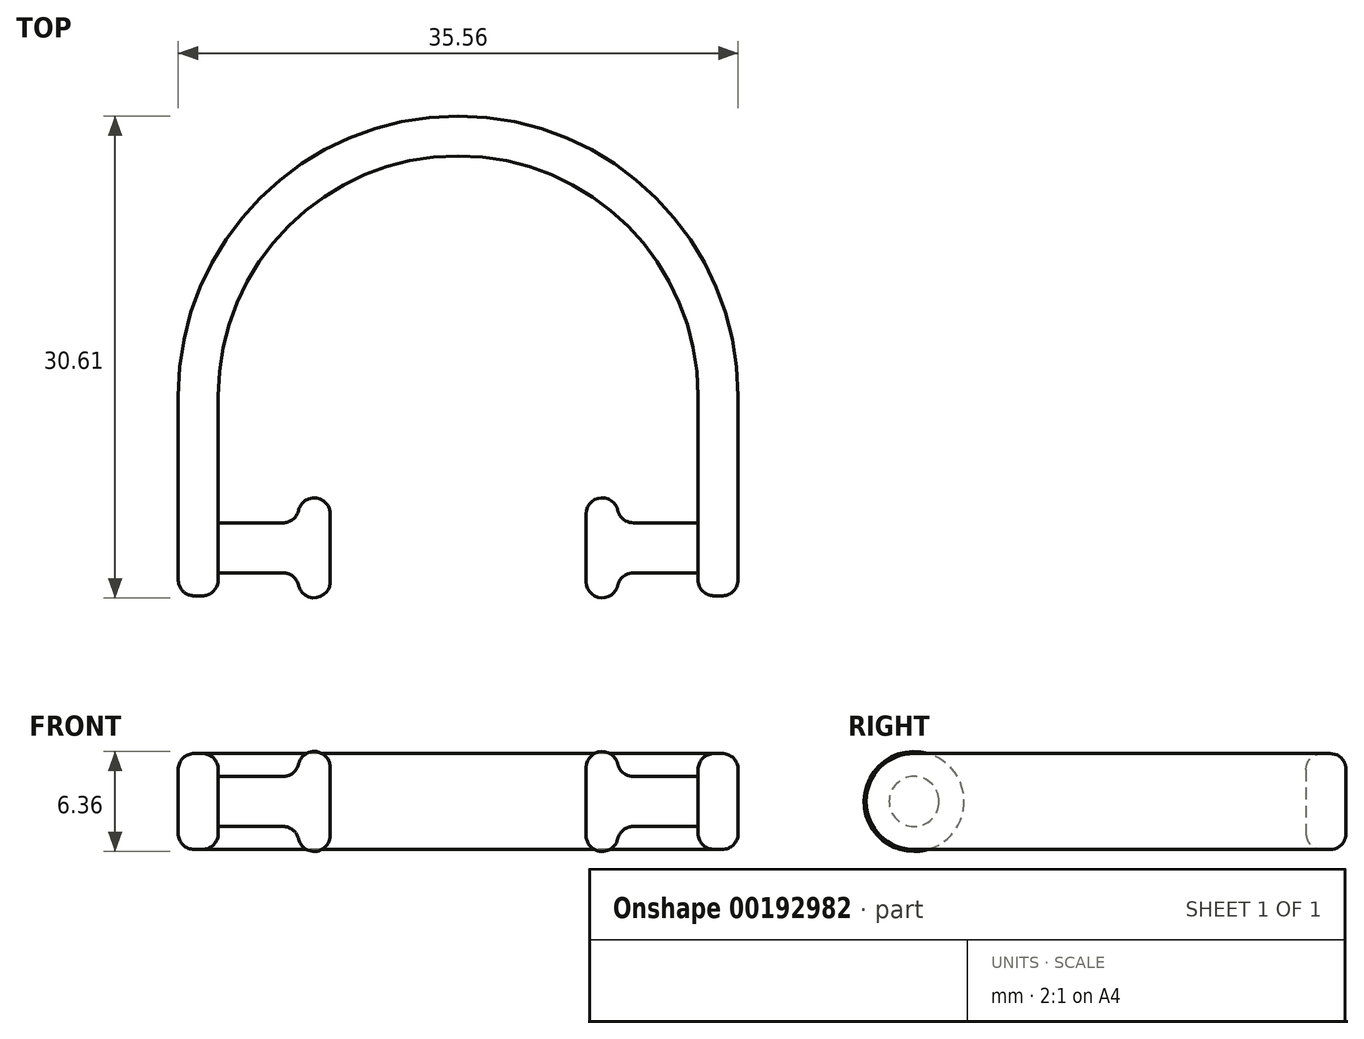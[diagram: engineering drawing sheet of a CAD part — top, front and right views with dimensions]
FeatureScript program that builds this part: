
annotation { "Feature Type Name" : "Feature", "Feature Type Description" : "" }
export const myFeature = defineFeature(function(context is Context, id is Id, definition is map)
    precondition{}
    {
        {
            var Q0;
            Q0=qCreatedBy(makeId("Top.planeOp"),FACE);
            var sketch = newSketch(context, id + "F0", { "sketchPlane" : qUnion([Q0])});
            skArc(sketch, "E0", {"start": v(-15.24, 9.65) * mm, "mid": v(0, 24.9) * mm, "end": v(15.24, 9.65) * mm});
            skLineSegment(sketch, "E1", {"start": v(-15.24, 9.65) * mm, "end": v(-15.24, -3.05) * mm});
            skLineSegment(sketch, "E2", {"start": v(-17.78, -3.05) * mm, "end": v(-17.78, 9.65) * mm});
            skLineSegment(sketch, "E3", {"start": v(0, 67.15) * mm, "end": v(0, -19.72) * mm, "construction": true});
            skLineSegment(sketch, "E4", {"start": v(-17.78, -3.05) * mm, "end": v(-15.24, -3.05) * mm});
            skLineSegment(sketch, "E5.MirrorCS", {"start": v(17.78, -3.05) * mm, "end": v(15.24, -3.05) * mm});
            skLineSegment(sketch, "E6.MirrorCS", {"start": v(15.24, 9.65) * mm, "end": v(15.24, -3.05) * mm});
            skLineSegment(sketch, "E7.MirrorCS", {"start": v(17.78, -3.05) * mm, "end": v(17.78, 9.65) * mm});
            skArc(sketch, "E8", {"start": v(-17.78, 9.65) * mm, "mid": v(0, 27.43) * mm, "end": v(17.78, 9.65) * mm});
            skSolve(sketch);
        }
        {
            var Q0;
            Q0=qSketchRegion(id+"F0",true);
            extrude(context, id + "F1", {"entities" : qUnion([Q0]), "endBound" : BoundingType.SYMMETRIC, "depth" : 6.1 * mm});
        }
        {
            var Q0;
            Q0=qCreatedBy(makeId("Top.planeOp"),FACE);
            var sketch = newSketch(context, id + "F2", { "sketchPlane" : qUnion([Q0])});
            skLineSegment(sketch, "E9", {"start": v(-15.24, 0) * mm, "end": v(-8.13, 0) * mm});
            skLineSegment(sketch, "E10", {"start": v(-8.13, 0) * mm, "end": v(-8.13, 3.18) * mm});
            skLineSegment(sketch, "E11", {"start": v(-8.13, 3.18) * mm, "end": v(-10.16, 3.18) * mm});
            skLineSegment(sketch, "E12", {"start": v(-10.16, 3.18) * mm, "end": v(-10.16, 1.59) * mm});
            skLineSegment(sketch, "E13", {"start": v(-10.16, 1.59) * mm, "end": v(-15.24, 1.59) * mm});
            skLineSegment(sketch, "E14", {"start": v(-15.24, 1.59) * mm, "end": v(-15.24, 0) * mm});
            skLineSegment(sketch, "E15", {"start": v(0, 27.07) * mm, "end": v(0, -22.76) * mm, "construction": true});
            skLineSegment(sketch, "E16.MirrorCS", {"start": v(15.24, 0) * mm, "end": v(8.13, 0) * mm});
            skLineSegment(sketch, "E17.MirrorCS", {"start": v(15.24, 1.59) * mm, "end": v(15.24, 0) * mm});
            skLineSegment(sketch, "E18.MirrorCS", {"start": v(10.16, 1.59) * mm, "end": v(15.24, 1.59) * mm});
            skLineSegment(sketch, "E19.MirrorCS", {"start": v(10.16, 3.18) * mm, "end": v(10.16, 1.59) * mm});
            skLineSegment(sketch, "E20.MirrorCS", {"start": v(43.07, 0) * mm, "end": v(-47.77, 0) * mm, "construction": true});
            skLineSegment(sketch, "E21.MirrorCS", {"start": v(8.13, 3.17) * mm, "end": v(10.16, 3.17) * mm});
            skLineSegment(sketch, "E22.MirrorCS", {"start": v(8.13, 0) * mm, "end": v(8.13, 3.18) * mm});
            skSolve(sketch);
        }
        {
            var Q0;
            Q0=qSketchRegion(id+"F2",true);
            var Q1;
            Q1=sQuery(id+"F2.wireOp",EDGE,"E20.MirrorCS");
            revolve(context, id + "F3", {"operationType" : NewBodyOperationType.ADD, "entities" : qUnion([Q0]), "axis" : qUnion([Q1]), "revolveType" : RevolveType.FULL});
        }
        {
            var Q0;
            Q0=makeQuery(id+"F1.opExtrude","CAP_EDGE",EDGE,{"disambiguationData":[OSD([sQuery(id+"F0.wireOp",EDGE,"E4")])],"isStart":true});
            var Q1;
            Q1=makeQuery(id+"F1.opExtrude","CAP_EDGE",EDGE,{"disambiguationData":[OSD([sQuery(id+"F0.wireOp",EDGE,"E4")])],"isStart":false});
            var Q2;
            Q2=makeQuery(id+"F1.opExtrude","CAP_EDGE",EDGE,{"disambiguationData":[OSD([sQuery(id+"F0.wireOp",EDGE,"E5.MirrorCS")])],"isStart":false});
            var Q3;
            Q3=makeQuery(id+"F1.opExtrude","CAP_EDGE",EDGE,{"disambiguationData":[OSD([sQuery(id+"F0.wireOp",EDGE,"E5.MirrorCS")])],"isStart":true});
            fillet(context, id + "F4", {"entities" : qUnion([Q0, Q1, Q2, Q3]), "radius" : 3.05 * mm, "allowEdgeOverflow" : false});
        }
        {
            var Q0;
            Q0=makeQuery(id+"F1.opExtrude","CAP_EDGE",EDGE,{"disambiguationData":[OSD([sQuery(id+"F0.wireOp",EDGE,"E8")])],"isStart":false});
            fillet(context, id + "F5", {"entities" : qUnion([Q0]), "radius" : 1.02 * mm, "tangentPropagation" : true, "allowEdgeOverflow" : false});
        }
        {
            var Q0;
            Q0=makeQuery(id+"F1.opExtrude","CAP_EDGE",EDGE,{"disambiguationData":[OSD([sQuery(id+"F0.wireOp",EDGE,"E0")])],"isStart":false});
            fillet(context, id + "F6", {"entities" : qUnion([Q0]), "radius" : 1.02 * mm, "tangentPropagation" : true, "allowEdgeOverflow" : false});
        }
        {
            var Q0;
            Q0=makeQuery(id+"F3.opRevolve","SWEPT_EDGE",EDGE,{"disambiguationData":[OSD([sQuery(id+"F2.wireOp",EDGE,"E10"),sQuery(id+"F2.wireOp",EDGE,"E11")])]});
            var Q1;
            Q1=makeQuery(id+"F3.opRevolve","SWEPT_EDGE",EDGE,{"disambiguationData":[OSD([sQuery(id+"F2.wireOp",EDGE,"E21.MirrorCS"),sQuery(id+"F2.wireOp",EDGE,"E22.MirrorCS")])]});
            var Q2;
            Q2=makeQuery(id+"F3.opRevolve","SWEPT_EDGE",EDGE,{"disambiguationData":[OSD([sQuery(id+"F2.wireOp",EDGE,"E11"),sQuery(id+"F2.wireOp",EDGE,"E12")])]});
            var Q3;
            Q3=makeQuery(id+"F3.opRevolve","SWEPT_EDGE",EDGE,{"disambiguationData":[OSD([sQuery(id+"F2.wireOp",EDGE,"E19.MirrorCS"),sQuery(id+"F2.wireOp",EDGE,"E21.MirrorCS")])]});
            fillet(context, id + "F7", {"entities" : qUnion([Q0, Q1, Q2, Q3]), "radius" : 1.02 * mm, "tangentPropagation" : true, "allowEdgeOverflow" : false});
        }
        {
            var Q0;
            Q0=makeQuery(id+"F3.opRevolve","SWEPT_EDGE",EDGE,{"disambiguationData":[OSD([sQuery(id+"F2.wireOp",EDGE,"E17.MirrorCS"),sQuery(id+"F2.wireOp",EDGE,"E18.MirrorCS")])]});
            var Q1;
            Q1=makeQuery(id+"F3.opRevolve","SWEPT_EDGE",EDGE,{"disambiguationData":[OSD([sQuery(id+"F2.wireOp",EDGE,"E12"),sQuery(id+"F2.wireOp",EDGE,"E13")])]});
            var Q2;
            Q2=makeQuery(id+"F3.opRevolve","SWEPT_EDGE",EDGE,{"disambiguationData":[OSD([sQuery(id+"F2.wireOp",EDGE,"E13"),sQuery(id+"F2.wireOp",EDGE,"E14")])]});
            var Q3;
            Q3=makeQuery(id+"F3.opRevolve","SWEPT_EDGE",EDGE,{"disambiguationData":[OSD([sQuery(id+"F2.wireOp",EDGE,"E18.MirrorCS"),sQuery(id+"F2.wireOp",EDGE,"E19.MirrorCS")])]});
            fillet(context, id + "F8", {"entities" : qUnion([Q0, Q1, Q2, Q3]), "radius" : 1.02 * mm, "tangentPropagation" : true, "allowEdgeOverflow" : false});
        }
    });
